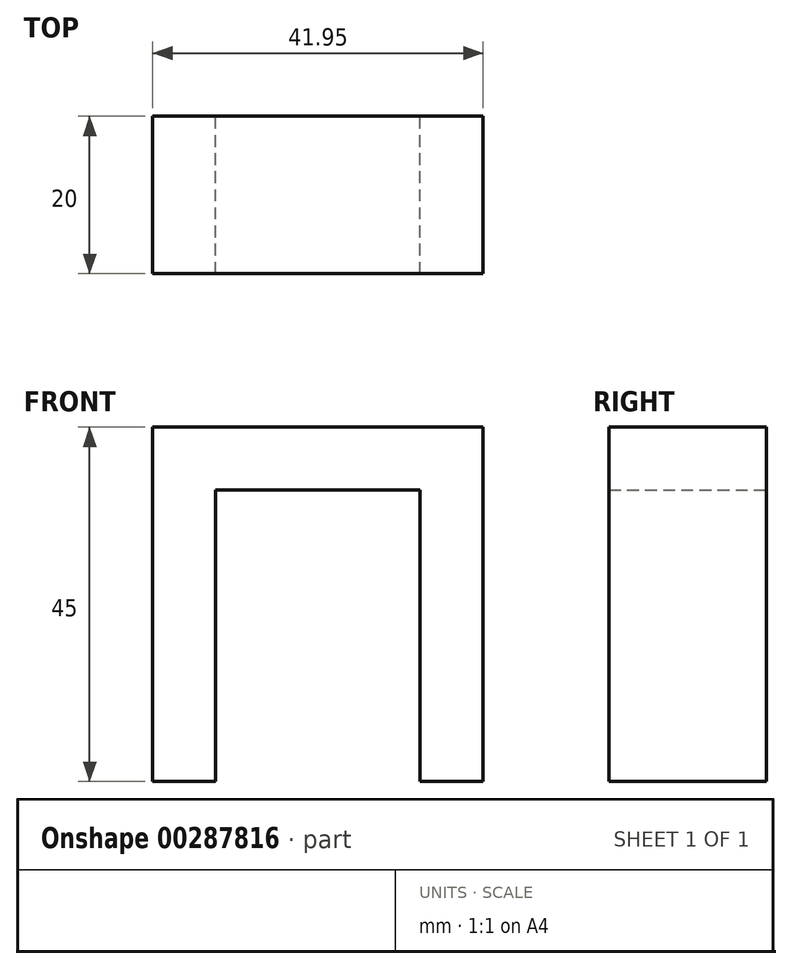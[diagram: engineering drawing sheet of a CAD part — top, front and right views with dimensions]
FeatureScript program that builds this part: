
annotation { "Feature Type Name" : "Feature", "Feature Type Description" : "" }
export const myFeature = defineFeature(function(context is Context, id is Id, definition is map)
    precondition{}
    {
        {
            var Q0;
            Q0=qCreatedBy(makeId("Front.planeOp"),FACE);
            var sketch = newSketch(context, id + "F0", { "sketchPlane" : qUnion([Q0])});
            skLineSegment(sketch, "E0", {"start": v(-17.3, 13.99) * mm, "end": v(-17.3, -23.01) * mm});
            skLineSegment(sketch, "E1", {"start": v(-17.3, 13.99) * mm, "end": v(8.66, 13.99) * mm});
            skLineSegment(sketch, "E2", {"start": v(8.66, 13.99) * mm, "end": v(8.66, -23.01) * mm});
            skLineSegment(sketch, "E3.0", {"start": v(-25.3, 21.99) * mm, "end": v(-25.3, -23.01) * mm});
            skLineSegment(sketch, "E3.1", {"start": v(-25.3, 21.99) * mm, "end": v(16.66, 21.99) * mm});
            skLineSegment(sketch, "E3.2", {"start": v(16.66, 21.99) * mm, "end": v(16.66, -23.01) * mm});
            skLineSegment(sketch, "E4", {"start": v(-17.3, -23.01) * mm, "end": v(-25.3, -23.01) * mm});
            skLineSegment(sketch, "E5", {"start": v(8.66, -23.01) * mm, "end": v(16.66, -23.01) * mm});
            skSolve(sketch);
        }
        {
            var Q0;
            Q0=makeQuery(id+"F0.imprint","IMPRINT",FACE,{"disambiguationData":[TD([[makeQuery(id+"F0.imprint","IMPRINT",EDGE,{"derivedFrom":sQuery(id+"F0.wireOp",EDGE,"E0")}),-1.0]])]});
            extrude(context, id + "F1", {"entities" : qUnion([Q0]), "depth" : 20 * mm});
        }
    });
